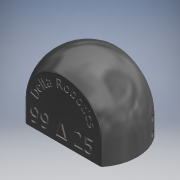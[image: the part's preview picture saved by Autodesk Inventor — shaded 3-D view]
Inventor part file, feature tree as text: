
AUTODESK INVENTOR PART (.ipt)
format: ipt  version: 2019 (Build 230136000, 136)  size: 730,624 bytes
history: native  units: mm (DEFAULTED — no unit token found)
features: sketch x10, extrude x9, plane x5, mirror x3, revolve x1, fillet x1
ambient origin geometry x8: Origin, YZ Plane, XZ Plane, XY Plane, X Axis, Y Axis, Z Axis, Center Point
bodies: Solid1 (feature_tree)
feature tree (29):
  extrude  "Extrusion1"  Depth=88.9mm
  extrude  "Extrusion2"  Depth=25.4mm
  extrude  "Extrusion3"  Depth=3.175mm TaperAngle=0.0deg
  plane  "Work Plane1"
  mirror  "Mirror1"
  plane  "Work Plane2"
  revolve  "Revolution1"  [1 undecoded]
  extrude  "Extrusion4"  Depth=44.45mm
  plane  "Work Plane3"
  mirror  "Mirror2"
  fillet  "Fillet1"  Radius=44.45mm
  sketch  "Sketch7"  dims[d14=180.0deg d15=25.4mm d16=0.0mm]
  extrude  "Extrusion5"  Depth=25.4mm TaperAngle=0.0deg
  extrude  "Extrusion6"  Depth=6.35mm
  plane  "Work Plane4"
  extrude  "Extrusion7"  Depth=8.001mm
  plane  "Work Plane5"
  mirror  "Mirror3"
  extrude  "Extrusion8"  Depth=6.35mm
  extrude  "Extrusion9"  Depth=3.048mm
  sketch  "Sketch1"  dims[d0=82.55mm d1=88.9mm]
  sketch  "Sketch2"  dims[d2=25.4mm d3=25.4mm]
  sketch  "Sketch3"  dims[d4=59.69mm d5=0.0mm d6=3.175mm d7=0.0mm]
  sketch  "Sketch5"  dims[d8=12.7mm d9=25.4mm]
  sketch  "Sketch6"  dims[d10=9.525mm d11=0.0mm d12=44.45mm d13=44.45mm]
  sketch  "Sketch8"  dims[d17=3.175mm d18=6.35mm]
  sketch  "Sketch9"  dims[d19=6.35mm d20=8.001mm]
  sketch  "Sketch10"  dims[d21=24.003mm d22=6.35mm]
  sketch  "Sketch11"  dims[d23=2.54mm d24=0.0mm d25=3.048mm d26=3.048mm d27=2.54mm d28=0.0mm d29=6.35mm d30=6.35mm d31=19.05mm d32=0.0mm d33=38.1mm d34=1.27mm d35=0.0mm d36=1.5875mm d37=0.0mm d38=3.175mm d39=3.175mm d40=3.175mm d41=19.05mm d42=12.7mm d43=12.7mm d44=12.7mm]
note: 1 required parameter value undecoded (feature->parameter linkage not recoverable at this tier; creation-order binding heuristic only, values carry confidence <= 0.55)
